# Revit family: Rohrschelle Titan HD, o.D, o.A., o.VS
name_source: partatom
category: HLS-Bauteile
revit_build: Autodesk Revit 2017 (Build: 20190507_1515(x64)
units: mm (PartAtom-declared; Revit-internal decimal feet)

## family parameters
Arbeitsebenenbasiert = Ja
Beim Laden mit Abzugskörper schneiden = Nein
Bemaßung runder Anschluss = Durchmesser verwenden
Gemeinsam genutzt = Ja
Immer vertikal = Nein
Raumberechnungspunkt = Nein
Teiletyp = Normal

## types (21) — shared parameters
A = 16 mm  [stored 0.0524934 ft]
Anschluss = ohne Anschluss
Bauart = zweiteilig
DF1 = 29 mm  [stored 0.0951444 ft]
DVS = 13 mm
Fabrikat = MEFA
Firma = MEFA Befestigungs- und Montagesysteme GmbH
HGA = 11 mm  [stored 0.0360892 ft]
MB = 50 mm  [stored 0.164042 ft]
MD = 5 mm  [stored 0.0164042 ft]
Material = Stahl
Materialmaße = 50x5,0 mm
Materialname = S235
Mengeneinheit = St
Oberflaeche = galvanisch verzinkt
Verschluss-Schraube = M12
Vorgabe-Ansicht = 1219 mm
max. zul. Last horizontal = 0.00 kN
max. zul. Last vertikal = 0.00 kN
zero-valued in all types: Nennweite DN Rohr, max. Rohraußendurchmesser, min. Rohraußendurchmesser

## per-type parameters (varying)
| type | Achsabstand | Artikelnummer | B | Brandschutz | Breite | Breite Material | D | DF2 | Gewicht | Gewicht pro Bauteil | H | Höhe | Kurztext1 | Kurztext2 | R | RM | Rohraußendurchmesser | Rohraußendurchmesser Zoll | S | Stärke Material | Verschluss | max. Höhe | max. zul. Last | vpe |
| Titan HD, M12, Ø 64, o.D., o.VS, o.AG. | 112 mm | 0070500 | 141 mm | RAL GZ 656 | 141 mm |  | 64 mm  [stored 0.209974 ft] | 13 mm | 0.61 kg | 0.61 kg | 85 mm  [stored 0.278871 ft] | 85 mm | Rohrschelle Titan HD 50x5,0 | 64 mm o.A. | 32 mm  [stored 0.104987 ft] | 37 mm  [stored 0.121391 ft] | 64 mm  [stored 0.209974 ft] | Zoll | 112 mm  [stored 0.367454 ft] | 0 mm  [stored 0 ft] | Schraubverschluss | 85 mm  [stored 0.278871 ft] | 6.00 kN | 1 St |
| Titan HD, M12, Ø 76, o.D., o.VS, o.AG. | 124 mm | 0070504 | 154 mm | RAL GZ 656 | 153 mm |  | 76 mm  [stored 0.249344 ft] | 13 mm | 0.69 kg | 0.69 kg | 97 mm  [stored 0.318241 ft] | 97 mm | Rohrschelle Titan HD 50x5,0 | 76 mm o.A. | 38 mm  [stored 0.124672 ft] | 43 mm | 76 mm  [stored 0.249344 ft] | 2 1/2 Zoll | 125 mm | 0 mm  [stored 0 ft] | Schraubverschluss | 97 mm  [stored 0.318241 ft] | 6.00 kN | 1 St |
| Titan HD, M12, Ø 89, o.D., o.VS, o.AG. | 138 mm | 0070506 | 167 mm | RAL GZ 656 | 167 mm |  | 89 mm  [stored 0.291995 ft] | 13 mm | 0.77 kg | 0.77 kg | 110 mm  [stored 0.360892 ft] | 110 mm | Rohrschelle Titan HD 50x5,0 | 89 mm M12 | 45 mm | 50 mm  [stored 0.164042 ft] | 89 mm  [stored 0.291995 ft] | 3 Zoll | 138 mm | 0 mm  [stored 0 ft] | Schraubverschluss | 110 mm  [stored 0.360892 ft] | 6.00 kN | 1 St |
| Titan HD, M12, Ø108, o.D., o.VS, o.AG. | 148 mm | 0070512 | 186 mm |  | 186 mm | 50 mm | 108 mm  [stored 0.354331 ft] | 13 mm | 0.89 kg | 0.89 kg | 129 mm |  | Rohrschelle Form A Titan HD 50x5 | 108 mm ohne Anschluss o. Dämm. | 54 mm  [stored 0.177165 ft] | 59 mm  [stored 0.19357 ft] | 108 mm  [stored 0.354331 ft] |  | 157 mm | 5 mm  [stored 0.0164042 ft] |  | 129 mm | 6.00 kN | 1 |
| Titan HD, M12, Ø110, o.D., o.VS, o.AG. | 159 mm | keine Artikelnummer vergeben | 188 mm | RAL GZ 656 | 188 mm |  | 110 mm  [stored 0.360892 ft] | 13 mm | 1.06 kg | 1.06 kg | 131 mm | 131 mm | Rohrschelle Titan HD 50x5,0 | 110 mm o.A. | 55 mm  [stored 0.180446 ft] | 60 mm  [stored 0.19685 ft] | 110 mm  [stored 0.360892 ft] | Zoll | 159 mm | 0 mm  [stored 0 ft] | Schraubverschluss | 131 mm | 6.00 kN | 1 St |
| Titan HD, M12, Ø133, o.D., o.VS, o.AG. | 173 mm | 0070581 | 212 mm |  | 212 mm | 50 mm | 133 mm | 14 mm  [stored 0.0459318 ft] | 1.05 kg | 1.05 kg | 154 mm |  | Rohrschelle Form A Titan HD 50x5 | 133 mm ohne Anschluss o. Dämm. | 67 mm | 72 mm | 133 mm |  | 183 mm | 5 mm  [stored 0.0164042 ft] |  | 154 mm | 6.00 kN | 1 |
| Titan HD, M12, Ø135, o.D., o.VS, o.AG. | 175 mm | 0070600 | 214 mm |  | 214 mm | 50 mm | 135 mm | 14 mm  [stored 0.0459318 ft] | 1.06 kg | 1.06 kg | 156 mm |  | Rohrschelle Form A Titan HD 50x5 | 135 mm ohne Anschluss o. Dämm. | 68 mm | 73 mm | 135 mm |  | 185 mm | 5 mm  [stored 0.0164042 ft] |  | 156 mm | 6.00 kN | 1 |
| Titan HD, M12, Ø140, o.D., o.VS, o.AG. | 180 mm | 0070603 | 219 mm |  | 219 mm | 50 mm | 140 mm | 14 mm  [stored 0.0459318 ft] | 1.09 kg | 1.09 kg | 161 mm |  | Rohrschelle Form A Titan HD 50x5 | 140 mm ohne Anschluss o. Dämm. | 70 mm  [stored 0.229659 ft] | 75 mm  [stored 0.246063 ft] | 140 mm |  | 190 mm | 5 mm  [stored 0.0164042 ft] |  | 161 mm | 6.00 kN | 1 |
| Titan HD, M12, Ø160, o.D., o.VS, o.AG. | 210 mm | 0070646 | 239 mm | RAL GZ 656 | 239 mm |  | 160 mm | 14 mm  [stored 0.0459318 ft] | 1.22 kg | 1.22 kg | 181 mm | 181 mm | Rohrschelle Titan HD 50x5,0 | 160 mm, o.A., o.D. | 80 mm  [stored 0.262467 ft] | 85 mm  [stored 0.278871 ft] | 160 mm | Zoll | 210 mm | 0 mm  [stored 0 ft] | Schraubverschluss | 181 mm | 6.00 kN | 1 St |
| Titan HD, M12, Ø165, o.D., o.VS, o.AG. | 205 mm | 0070686 | 244 mm |  | 244 mm | 50 mm | 165 mm | 14 mm  [stored 0.0459318 ft] | 1.25 kg | 1.25 kg | 186 mm |  | Rohrschelle Form A Titan HD 50x5 | 165 mm ohne Anschluss o. Dämm. | 83 mm | 88 mm | 165 mm |  | 215 mm | 5 mm  [stored 0.0164042 ft] |  | 186 mm | 6.00 kN | 1 |
| Titan HD, M12, Ø168, o.D., o.VS, o.AG. | 208 mm | 0070689 | 247 mm |  | 247 mm | 50 mm | 168 mm | 14 mm  [stored 0.0459318 ft] | 1.27 kg | 1.27 kg | 189 mm |  | Rohrschelle Form A Titan HD 50x5 | 168 mm ohne Anschluss o. Dämm. | 84 mm  [stored 0.275591 ft] | 89 mm  [stored 0.291995 ft] | 168 mm |  | 218 mm | 5 mm  [stored 0.0164042 ft] |  | 189 mm | 6.00 kN | 1 |
| Titan HD, M12, Ø194, o.D., o.VS, o.AG. | 234 mm | 0070751 | 273 mm |  | 273 mm | 50 mm | 194 mm | 14 mm  [stored 0.0459318 ft] | 1.44 kg | 1.44 kg | 215 mm |  | Rohrschelle Form A Titan HD 50x5 | 164 mm ohne Anschluss o. Dämm. | 97 mm  [stored 0.318241 ft] | 102 mm  [stored 0.334646 ft] | 164 mm |  | 244 mm | 5 mm  [stored 0.0164042 ft] |  | 215 mm | 16.00 kN | 1 |
| Titan HD, M12, Ø200, o.D., o.VS, o.AG. | 240 mm | 0070778 | 279 mm |  | 279 mm | 50 mm | 200 mm | 14 mm  [stored 0.0459318 ft] | 1.47 kg | 1.47 kg | 221 mm |  | Rohrschelle Form A Titan HD 50x5 | 200 mm ohne Anschluss o. Dämm. | 100 mm  [stored 0.328084 ft] | 105 mm  [stored 0.344488 ft] | 200 mm |  | 250 mm | 5 mm  [stored 0.0164042 ft] |  | 221 mm | 16.00 kN | 1 |
| Titan HD, M12, Ø210, o.D., o.VS, o.AG. | 250 mm | 0070786 | 290 mm |  | 290 mm | 50 mm | 210 mm | 14 mm  [stored 0.0459318 ft] | 1.54 kg | 1.54 kg | 231 mm |  | Rohrschelle Form A Titan HD 50x5 | 210 mm ohne Anschluss o. Dämm. | 105 mm  [stored 0.344488 ft] | 110 mm  [stored 0.360892 ft] | 210 mm |  | 261 mm | 5 mm  [stored 0.0164042 ft] |  | 231 mm | 16.00 kN | 1 |
| Titan HD, M12, Ø219, o.D., o.VS, o.AG. | 260 mm | 0070808 | 299 mm |  | 299 mm | 50 mm | 219 mm | 14 mm  [stored 0.0459318 ft] | 1.59 kg | 1.59 kg | 240 mm |  | Rohrschelle Form A Titan HD 50x5 | 219 mm ohne Anschluss o. Dämm. | 110 mm  [stored 0.360892 ft] | 115 mm | 219 mm |  | 270 mm | 5 mm  [stored 0.0164042 ft] |  | 240 mm | 16.00 kN | 1 |
| Titan HD, M12, Ø267, o.D., o.VS, o.AG. | 307 mm | 0070881 | 347 mm |  | 347 mm | 50 mm | 267 mm | 14 mm  [stored 0.0459318 ft] | 1.90 kg | 1.90 kg | 288 mm |  | Rohrschelle Form A Titan HD 50x5 | 267 mm ohne Anschluss o. Dämm. | 134 mm | 139 mm | 267 mm |  | 318 mm | 5 mm  [stored 0.0164042 ft] |  | 288 mm | 16.00 kN | 1 |
| Titan HD, M12, Ø273, o.D., o.VS, o.AG. | 314 mm | 0070891 | 353 mm |  | 353 mm | 50 mm | 273 mm | 14 mm  [stored 0.0459318 ft] | 1.94 kg | 1.94 kg | 294 mm |  | Rohrschelle Form A Titan HD 50x5 | 273 mm ohne Anschluss o. Dämm. | 137 mm | 142 mm | 273 mm |  | 324 mm | 5 mm  [stored 0.0164042 ft] |  | 294 mm | 16.00 kN | 1 |
| Titan HD, M12, Ø324, o.D., o.VS, o.AG. | 364 mm | 0070945 | 404 mm |  | 404 mm | 50 mm | 324 mm | 14 mm  [stored 0.0459318 ft] | 2.26 kg | 2.26 kg | 345 mm |  | Rohrschelle Form A Titan HD 50x5 | 324 mm ohne Anschluss o. Dämm. | 162 mm | 167 mm | 324 mm |  | 375 mm | 5 mm  [stored 0.0164042 ft] |  | 345 mm | 16.00 kN | 1 |
| Titan HD, M12, Ø356, o.D., o.VS, o.AG. | 396 mm | 0070962 | 436 mm |  | 436 mm | 50 mm | 356 mm | 14 mm  [stored 0.0459318 ft] | 2.47 kg | 2.47 kg | 377 mm |  | Rohrschelle Form A Titan HD 50x5 | 356 mm ohne Anschluss o. Dämm. | 178 mm | 183 mm | 365 mm |  | 407 mm | 5 mm  [stored 0.0164042 ft] |  | 377 mm | 16.00 kN | 1 |
| Titan HD, M12, Ø368, o.D., o.VS, o.AG. | 408 mm | 0070964 | 448 mm |  | 448 mm | 50 mm | 368 mm | 14 mm  [stored 0.0459318 ft] | 2.54 kg | 2.54 kg | 389 mm |  | Rohrschelle Form A Titan HD 50x5 | 368 mm ohne Anschluss o. Dämm. | 184 mm | 189 mm | 368 mm |  | 419 mm | 5 mm  [stored 0.0164042 ft] |  | 389 mm | 16.00 kN | 1 |
| Titan HD, M12, Ø114, o.D., o.VS, o.AG. | 154 mm | 0070514 | 192 mm |  | 188 mm | 50 mm | 114 mm | 13 mm | 0.93 kg | 0.93 kg | 135 mm |  | Rohrschelle Form A Titan HD 50x5 | 114 mm ohne Anschluss o. Dämm. | 57 mm  [stored 0.187008 ft] | 62 mm  [stored 0.203412 ft] | 114 mm |  | 163 mm | 5 mm  [stored 0.0164042 ft] |  | 131 mm | 6.00 kN | 1 |

note: [stored X ft] marks values corroborated as IEEE doubles in the binary element streams (Revit-internal decimal feet)
